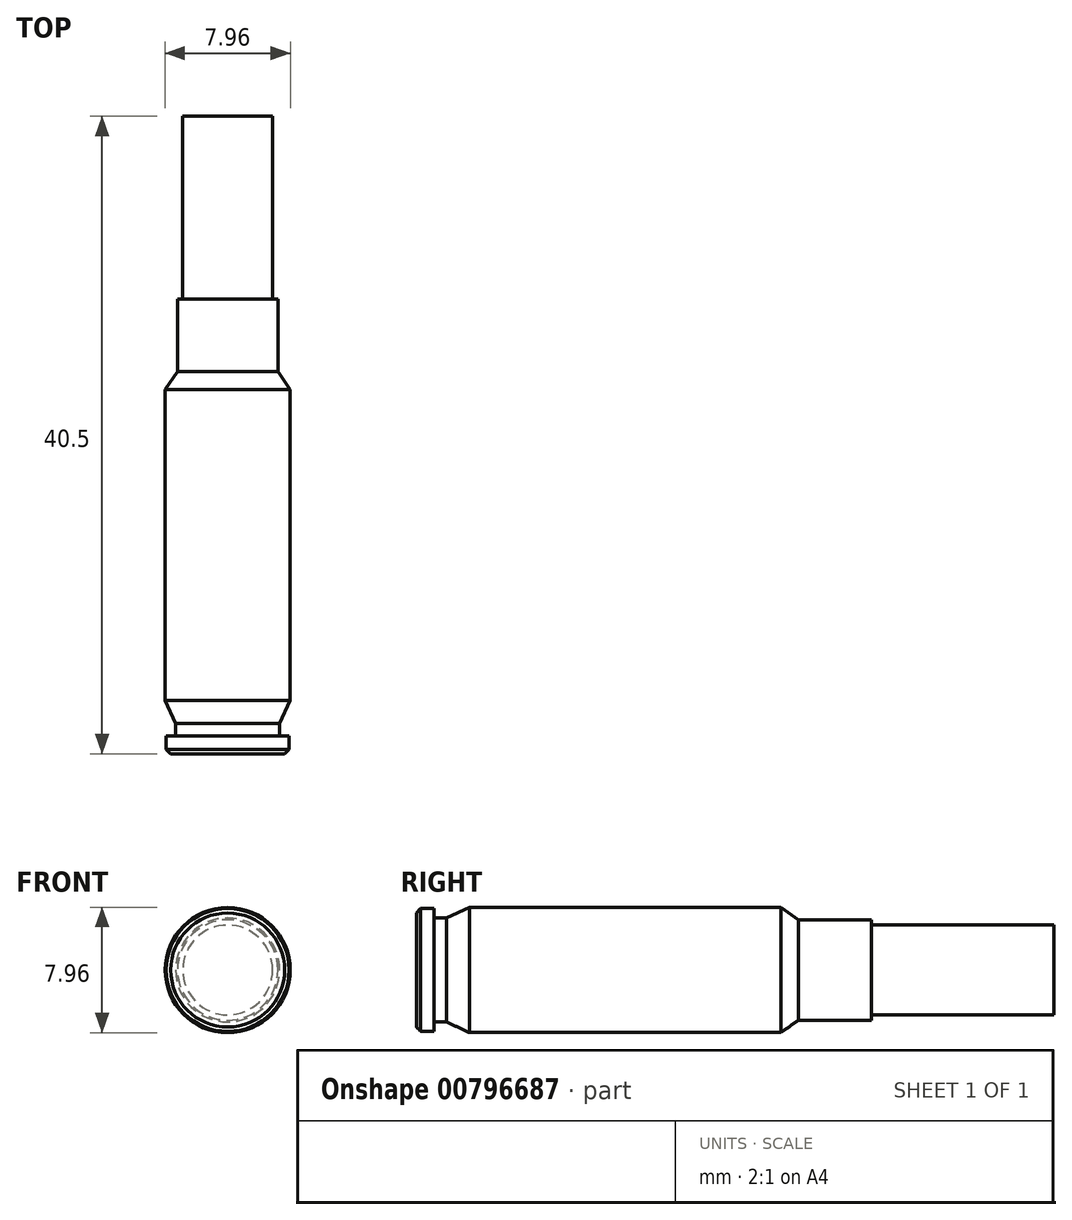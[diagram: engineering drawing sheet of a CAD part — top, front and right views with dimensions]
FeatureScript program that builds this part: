
annotation { "Feature Type Name" : "Feature", "Feature Type Description" : "" }
export const myFeature = defineFeature(function(context is Context, id is Id, definition is map)
    precondition{}
    {
        {
            var Q0;
            Q0=qCreatedBy(makeId("Right.planeOp"),FACE);
            var sketch = newSketch(context, id + "F0", { "sketchPlane" : qUnion([Q0])});
            skLineSegment(sketch, "E0", {"start": v(0, 0) * mm, "end": v(0.28, 0) * mm});
            skLineSegment(sketch, "E1", {"start": v(0.28, 0) * mm, "end": v(1.14, 0) * mm});
            skLineSegment(sketch, "E2", {"start": v(1.14, 0) * mm, "end": v(1.93, 0) * mm});
            skLineSegment(sketch, "E3", {"start": v(1.93, 0) * mm, "end": v(3.38, 0) * mm});
            skLineSegment(sketch, "E4", {"start": v(0, -4.34) * mm, "end": v(3.38, -4.34) * mm});
            skLineSegment(sketch, "E5", {"start": v(0, -5.92) * mm, "end": v(23.15, -5.92) * mm});
            skLineSegment(sketch, "E6", {"start": v(3.38, 0) * mm, "end": v(23.15, 0) * mm});
            skLineSegment(sketch, "E7", {"start": v(0, -7.77) * mm, "end": v(24.27, -7.77) * mm});
            skLineSegment(sketch, "E8", {"start": v(23.15, 0) * mm, "end": v(24.27, 0) * mm});
            skLineSegment(sketch, "E9", {"start": v(0, -9.96) * mm, "end": v(28.9, -9.96) * mm});
            skLineSegment(sketch, "E10", {"start": v(24.27, 0) * mm, "end": v(28.9, 0) * mm});
            skLineSegment(sketch, "E11", {"start": v(0, -13.1) * mm, "end": v(40.5, -13.1) * mm});
            skLineSegment(sketch, "E12", {"start": v(28.9, 0) * mm, "end": v(40.5, 0) * mm});
            skLineSegment(sketch, "E13", {"start": v(40.5, 0) * mm, "end": v(40.5, 2.85) * mm});
            skLineSegment(sketch, "E14", {"start": v(40.5, 2.85) * mm, "end": v(28.9, 2.85) * mm});
            skLineSegment(sketch, "E15", {"start": v(28.9, 0) * mm, "end": v(28.9, 3.19) * mm});
            skLineSegment(sketch, "E16", {"start": v(28.9, 3.19) * mm, "end": v(24.27, 3.19) * mm});
            skLineSegment(sketch, "E17", {"start": v(23.15, 0) * mm, "end": v(23.15, 3.98) * mm});
            skLineSegment(sketch, "E18", {"start": v(23.15, 3.98) * mm, "end": v(24.27, 3.2) * mm});
            skLineSegment(sketch, "E19", {"start": v(23.15, 3.98) * mm, "end": v(3.38, 3.98) * mm});
            skLineSegment(sketch, "E20", {"start": v(1.93, 0) * mm, "end": v(1.93, 3.3) * mm});
            skLineSegment(sketch, "E21", {"start": v(1.93, 3.3) * mm, "end": v(3.38, 3.98) * mm});
            skLineSegment(sketch, "E22", {"start": v(1.93, 3.3) * mm, "end": v(1.14, 3.3) * mm});
            skLineSegment(sketch, "E23", {"start": v(1.14, 0) * mm, "end": v(1.14, 3.9) * mm});
            skLineSegment(sketch, "E24", {"start": v(1.14, 3.9) * mm, "end": v(0.28, 3.9) * mm});
            skLineSegment(sketch, "E25", {"start": v(0, 0) * mm, "end": v(0, 3.62) * mm});
            skLineSegment(sketch, "E26", {"start": v(0, 3.62) * mm, "end": v(0.28, 3.9) * mm});
            skLineSegment(sketch, "E27", {"start": v(0.28, 3.9) * mm, "end": v(-0.12, 3.9) * mm});
            skLineSegment(sketch, "E28", {"start": v(0, 4.92) * mm, "end": v(1.93, 4.92) * mm});
            skSolve(sketch);
        }
        {
            var Q0;
            Q0=makeQuery(id+"F0.imprint","IMPRINT",FACE,{"disambiguationData":[TD([[makeQuery(id+"F0.imprint","IMPRINT",EDGE,{"derivedFrom":sQuery(id+"F0.wireOp",EDGE,"E0")}),1.0]])]});
            var Q1;
            {var subQ0=sQuery(id+"F0.wireOp",EDGE,"E2");Q1=makeQuery(id+"F0.imprint","IMPRINT",FACE,{"disambiguationData":[TD([[makeQuery(id+"F0.imprint","IMPRINT",EDGE,{"derivedFrom":subQ0}),1.0]])]});}
            var Q2;
            Q2=makeQuery(id+"F0.imprint","IMPRINT",FACE,{"disambiguationData":[TD([[makeQuery(id+"F0.imprint","IMPRINT",EDGE,{"derivedFrom":sQuery(id+"F0.wireOp",EDGE,"E3")}),1.0]])]});
            var Q3;
            Q3=makeQuery(id+"F0.imprint","IMPRINT",FACE,{"disambiguationData":[TD([[makeQuery(id+"F0.imprint","IMPRINT",EDGE,{"derivedFrom":sQuery(id+"F0.wireOp",EDGE,"E8")}),1.0]])]});
            var Q4;
            {var subQ0=sQuery(id+"F0.wireOp",EDGE,"E12");Q4=makeQuery(id+"F0.imprint","IMPRINT",FACE,{"disambiguationData":[TD([[makeQuery(id+"F0.imprint","IMPRINT",EDGE,{"derivedFrom":subQ0}),1.0]])]});}
            var Q5;
            Q5=sQuery(id+"F0.wireOp",EDGE,"E6");
            revolve(context, id + "F1", {"surfaceOperationType" : NewSurfaceOperationType.NEW, "entities" : qUnion([Q0, Q1, Q2, Q3, Q4]), "axis" : qUnion([Q5]), "revolveType" : RevolveType.FULL});
        }
    });
